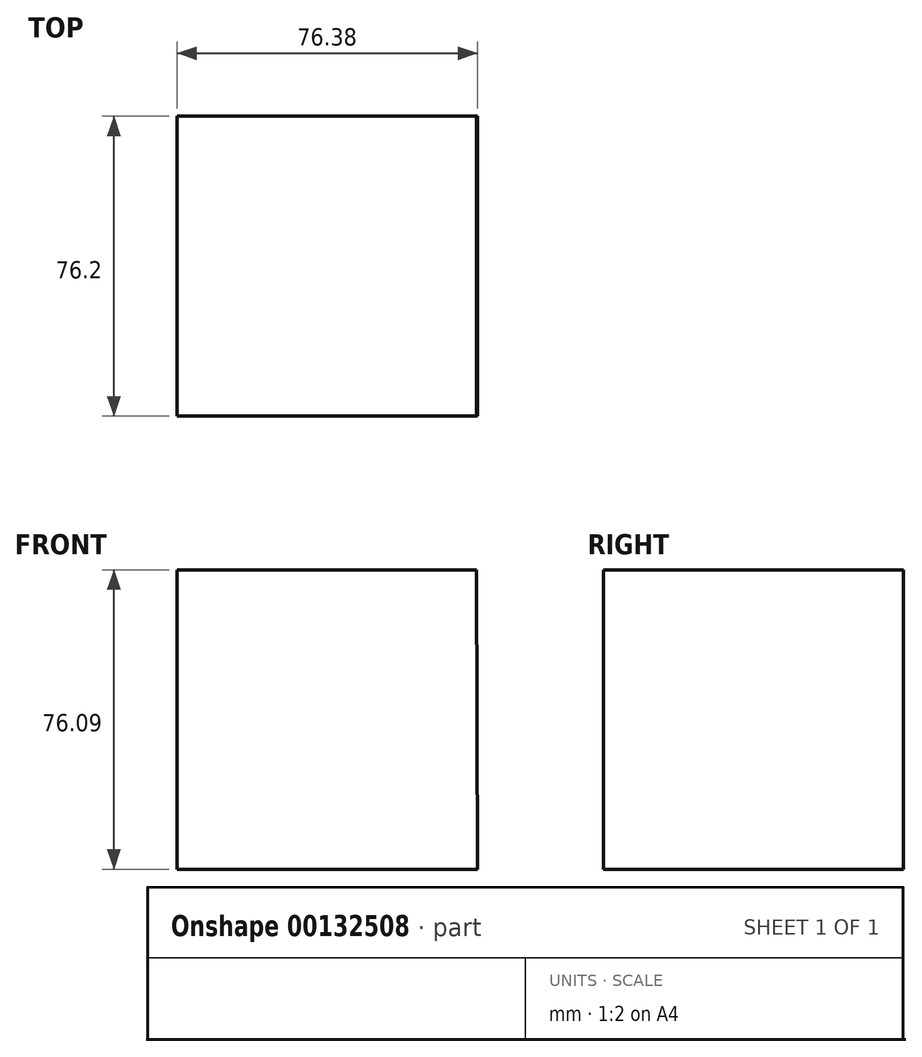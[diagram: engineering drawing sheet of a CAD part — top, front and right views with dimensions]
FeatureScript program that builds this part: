
annotation { "Feature Type Name" : "Feature", "Feature Type Description" : "" }
export const myFeature = defineFeature(function(context is Context, id is Id, definition is map)
    precondition{}
    {
        {
            var Q0;
            Q0=qCreatedBy(makeId("Front.planeOp"),FACE);
            var sketch = newSketch(context, id + "F0", { "sketchPlane" : qUnion([Q0])});
            skLineSegment(sketch, "E0", {"start": v(0, 0) * mm, "end": v(76.1, 0) * mm});
            skLineSegment(sketch, "E1", {"start": v(0, 0) * mm, "end": v(0, -76.1) * mm});
            skLineSegment(sketch, "E2", {"start": v(0, -76.1) * mm, "end": v(76.38, -76.1) * mm});
            skLineSegment(sketch, "E3", {"start": v(76.1, 0) * mm, "end": v(76.38, -76.1) * mm});
            skSolve(sketch);
        }
        {
            var Q0;
            Q0=makeQuery(id+"F0.imprint","IMPRINT",FACE,{"disambiguationData":[TD([[makeQuery(id+"F0.imprint","IMPRINT",EDGE,{"derivedFrom":sQuery(id+"F0.wireOp",EDGE,"E0")}),-1.0]])]});
            extrude(context, id + "F1", {"entities" : qUnion([Q0]), "depth" : 76.2 * mm});
        }
    });
